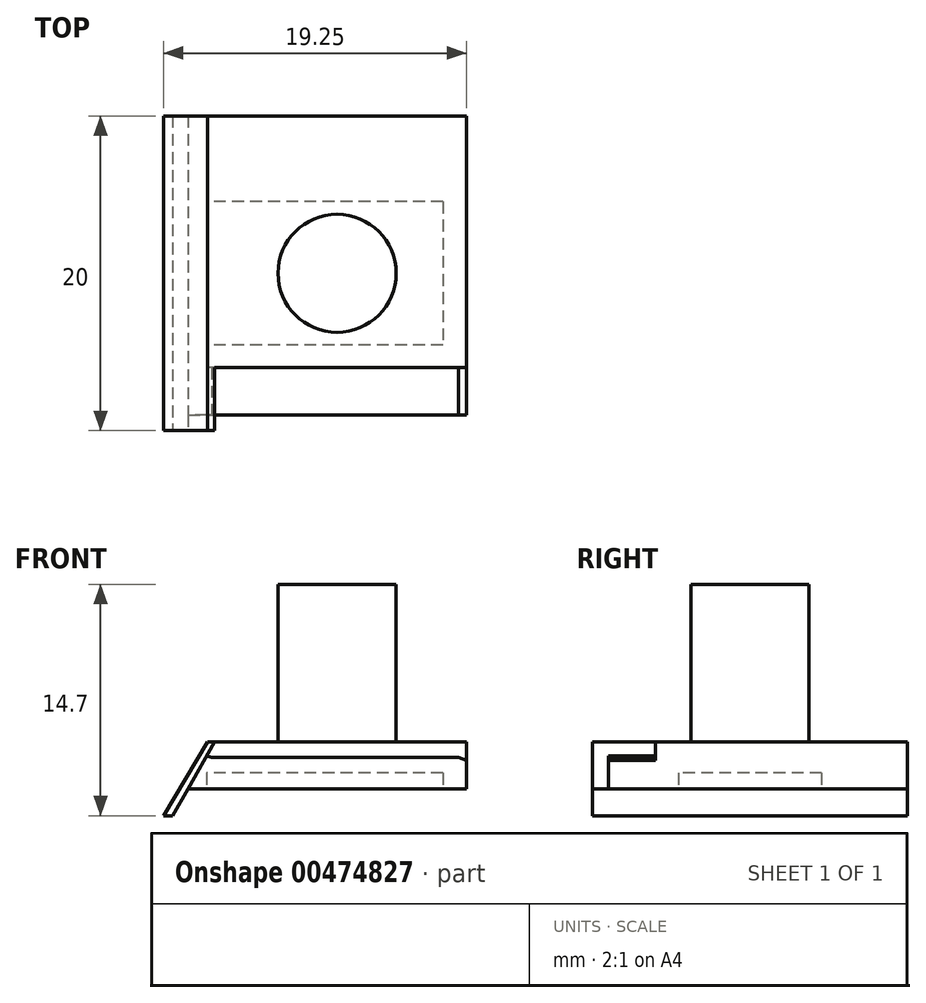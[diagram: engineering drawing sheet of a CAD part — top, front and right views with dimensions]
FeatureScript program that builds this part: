
annotation { "Feature Type Name" : "Feature", "Feature Type Description" : "" }
export const myFeature = defineFeature(function(context is Context, id is Id, definition is map)
    precondition{}
    {
        {
            var Q0;
            Q0=qCreatedBy(makeId("Front.planeOp"),FACE);
            var sketch = newSketch(context, id + "F0", { "sketchPlane" : qUnion([Q0])});
            skLineSegment(sketch, "E0", {"start": v(-19.25, -1.7) * mm, "end": v(-16.45, 3) * mm});
            skLineSegment(sketch, "E1", {"start": v(-16.45, 3) * mm, "end": v(0, 3) * mm});
            skLineSegment(sketch, "E2", {"start": v(0, 3) * mm, "end": v(0, 0) * mm});
            skLineSegment(sketch, "E3", {"start": v(0, 0) * mm, "end": v(-17.08, 0) * mm});
            skLineSegment(sketch, "E4", {"start": v(-17.08, 0) * mm, "end": v(-18.09, -1.7) * mm});
            skLineSegment(sketch, "E5", {"start": v(-18.09, -1.7) * mm, "end": v(-19.25, -1.7) * mm});
            skSolve(sketch);
        }
        {
            var Q0;
            Q0=makeQuery(id+"F0.imprint","IMPRINT",FACE,{"disambiguationData":[TD([[makeQuery(id+"F0.imprint","IMPRINT",EDGE,{"derivedFrom":sQuery(id+"F0.wireOp",EDGE,"E0")}),-1.0]])]});
            extrude(context, id + "F1", {"entities" : qUnion([Q0]), "depth" : 20 * mm});
        }
        {
            var Q0;
            Q0=makeQuery(id+"F1.opExtrude","CAP_FACE",FACE,{"disambiguationData":[OSD([sQuery(id+"F0.wireOp",EDGE,"E0"),sQuery(id+"F0.wireOp",EDGE,"E1"),sQuery(id+"F0.wireOp",EDGE,"E2"),sQuery(id+"F0.wireOp",EDGE,"E3"),sQuery(id+"F0.wireOp",EDGE,"E4"),sQuery(id+"F0.wireOp",EDGE,"E5")])],"isStart":false});
            var sketch = newSketch(context, id + "F2", { "sketchPlane" : qUnion([Q0])});
            skLineSegment(sketch, "E6", {"start": v(-0.5, 2) * mm, "end": v(0, 1.82) * mm});
            skLineSegment(sketch, "E7", {"start": v(0, 1.82) * mm, "end": v(0, 3) * mm});
            skLineSegment(sketch, "E8", {"start": v(0, 3) * mm, "end": v(-16, 3) * mm});
            skLineSegment(sketch, "E9", {"start": v(-0.5, 2) * mm, "end": v(-16.2, 2) * mm});
            skLineSegment(sketch, "E10", {"start": v(-16.2, 2) * mm, "end": v(-16.5, 2.1) * mm});
            skLineSegment(sketch, "E11", {"start": v(-16, 3) * mm, "end": v(-16.5, 2.1) * mm});
            skSolve(sketch);
        }
        {
            var Q0;
            Q0=qSketchRegion(id+"F2",true);
            extrude(context, id + "F3", {"entities" : qUnion([Q0]), "operationType" : NewBodyOperationType.REMOVE, "oppositeDirection" : true, "depth" : 4 * mm});
        }
        {
            var Q0;
            Q0=makeQuery(id+"F1.opExtrude","CAP_FACE",FACE,{"disambiguationData":[OSD([sQuery(id+"F0.wireOp",EDGE,"E0"),sQuery(id+"F0.wireOp",EDGE,"E1"),sQuery(id+"F0.wireOp",EDGE,"E2"),sQuery(id+"F0.wireOp",EDGE,"E3"),sQuery(id+"F0.wireOp",EDGE,"E4"),sQuery(id+"F0.wireOp",EDGE,"E5")])],"isStart":false});
            var sketch = newSketch(context, id + "F4", { "sketchPlane" : qUnion([Q0])});
            skLineSegment(sketch, "E12", {"start": v(0, 1.82) * mm, "end": v(-0.5, 2) * mm});
            skLineSegment(sketch, "E13", {"start": v(-0.5, 2) * mm, "end": v(-16.2, 2) * mm});
            skLineSegment(sketch, "E14", {"start": v(-16.2, 2) * mm, "end": v(-16.5, 2.1) * mm});
            skLineSegment(sketch, "E15", {"start": v(-16.5, 2.1) * mm, "end": v(-17.68, 0) * mm});
            skLineSegment(sketch, "E16", {"start": v(-17.68, 0) * mm, "end": v(0, 0) * mm});
            skLineSegment(sketch, "E17", {"start": v(0, 0) * mm, "end": v(0, 1.82) * mm});
            skSolve(sketch);
        }
        {
            var Q0;
            Q0=qSketchRegion(id+"F4",true);
            extrude(context, id + "F5", {"entities" : qUnion([Q0]), "operationType" : NewBodyOperationType.REMOVE, "oppositeDirection" : true, "depth" : 1 * mm});
        }
        {
            var Q0;
            Q0=makeQuery(id+"F1.opExtrude","CAP_FACE",FACE,{"disambiguationData":[OSD([sQuery(id+"F0.wireOp",EDGE,"E0"),sQuery(id+"F0.wireOp",EDGE,"E1"),sQuery(id+"F0.wireOp",EDGE,"E2"),sQuery(id+"F0.wireOp",EDGE,"E3"),sQuery(id+"F0.wireOp",EDGE,"E4"),sQuery(id+"F0.wireOp",EDGE,"E5")])],"isStart":false});
            var sketch = newSketch(context, id + "F6", { "sketchPlane" : qUnion([Q0])});
            skLineSegment(sketch, "E18", {"start": v(-18.09, -1.7) * mm, "end": v(-17.08, 0) * mm});
            skLineSegment(sketch, "E19", {"start": v(-17.08, 0) * mm, "end": v(-17.68, 0) * mm});
            skLineSegment(sketch, "E20", {"start": v(-17.68, 0) * mm, "end": v(-18.67, -1.7) * mm});
            skLineSegment(sketch, "E21", {"start": v(-18.67, -1.7) * mm, "end": v(-18.09, -1.7) * mm});
            skSolve(sketch);
        }
        {
            var Q0;
            Q0=qSketchRegion(id+"F6",true);
            extrude(context, id + "F7", {"entities" : qUnion([Q0]), "operationType" : NewBodyOperationType.REMOVE, "endBound" : BoundingType.THROUGH_ALL, "oppositeDirection" : true, "depth" : 25 * mm});
        }
        {
            var Q0;
            Q0=makeQuery(id+"F1.opExtrude","SWEPT_FACE",FACE,{"disambiguationData":[OSD([sQuery(id+"F0.wireOp",EDGE,"E1")])]});
            var sketch = newSketch(context, id + "F8", { "sketchPlane" : qUnion([Q0])});
            skLineSegment(sketch, "E22", {"start": v(-16.45, -20) * mm, "end": v(-16.45, 0) * mm, "construction": true});
            skPoint(sketch, "E23", {"position": v(-16.45, -10) * mm});
            skLineSegment(sketch, "E24", {"start": v(-16.45, -10) * mm, "end": v(0, -10) * mm, "construction": true});
            skCircle(sketch, "E25", {"center": v(-8.22, -10) * mm, "radius": 3.75 * mm});
            skSolve(sketch);
        }
        {
            var Q0;
            Q0=sQuery(id+"F8.wireOp",EDGE,"E24");
            cPlane(context, id + "F9", {"entities" : qUnion([Q0]), "cplaneType" : CPlaneType.LINE_ANGLE, "offset" : 25 * mm, "angle" : 0 * degree, "width" : 150 * mm, "height" : 150 * mm});
        }
        {
            var Q0;
            Q0=makeQuery(id+"F7.boolean.opBoolean","MERGE",FACE,{"derivedFrom":[makeQuery(id+"F1.opExtrude","SWEPT_FACE",FACE,{"disambiguationData":[OSD([sQuery(id+"F0.wireOp",EDGE,"E3")])]}),makeQuery(id+"F7.opExtrude","SWEPT_FACE",FACE,{"disambiguationData":[OSD([sQuery(id+"F6.wireOp",EDGE,"E19")])]})]});
            var sketch = newSketch(context, id + "F10", { "sketchPlane" : qUnion([Q0])});
            skLineSegment(sketch, "E26.bottom", {"start": v(-1.5, 5.45) * mm, "end": v(-16.5, 5.45) * mm});
            skLineSegment(sketch, "E26.top", {"start": v(-1.5, 14.55) * mm, "end": v(-16.5, 14.55) * mm});
            skLineSegment(sketch, "E26.left", {"start": v(-1.5, 5.45) * mm, "end": v(-1.5, 14.55) * mm});
            skLineSegment(sketch, "E26.right", {"start": v(-16.5, 5.45) * mm, "end": v(-16.5, 14.55) * mm});
            skSolve(sketch);
        }
        {
            var Q0;
            Q0=qSketchRegion(id+"F10",true);
            extrude(context, id + "F11", {"entities" : qUnion([Q0]), "operationType" : NewBodyOperationType.REMOVE, "oppositeDirection" : true, "depth" : 1 * mm});
        }
        {
            var Q0;
            Q0 = qSketchRegion(id + "F8", true);
            extrude(context, id + "F12", {"entities" : qUnion([Q0]), "operationType" : NewBodyOperationType.ADD, "depth" : 10 * mm});
        }
    });
